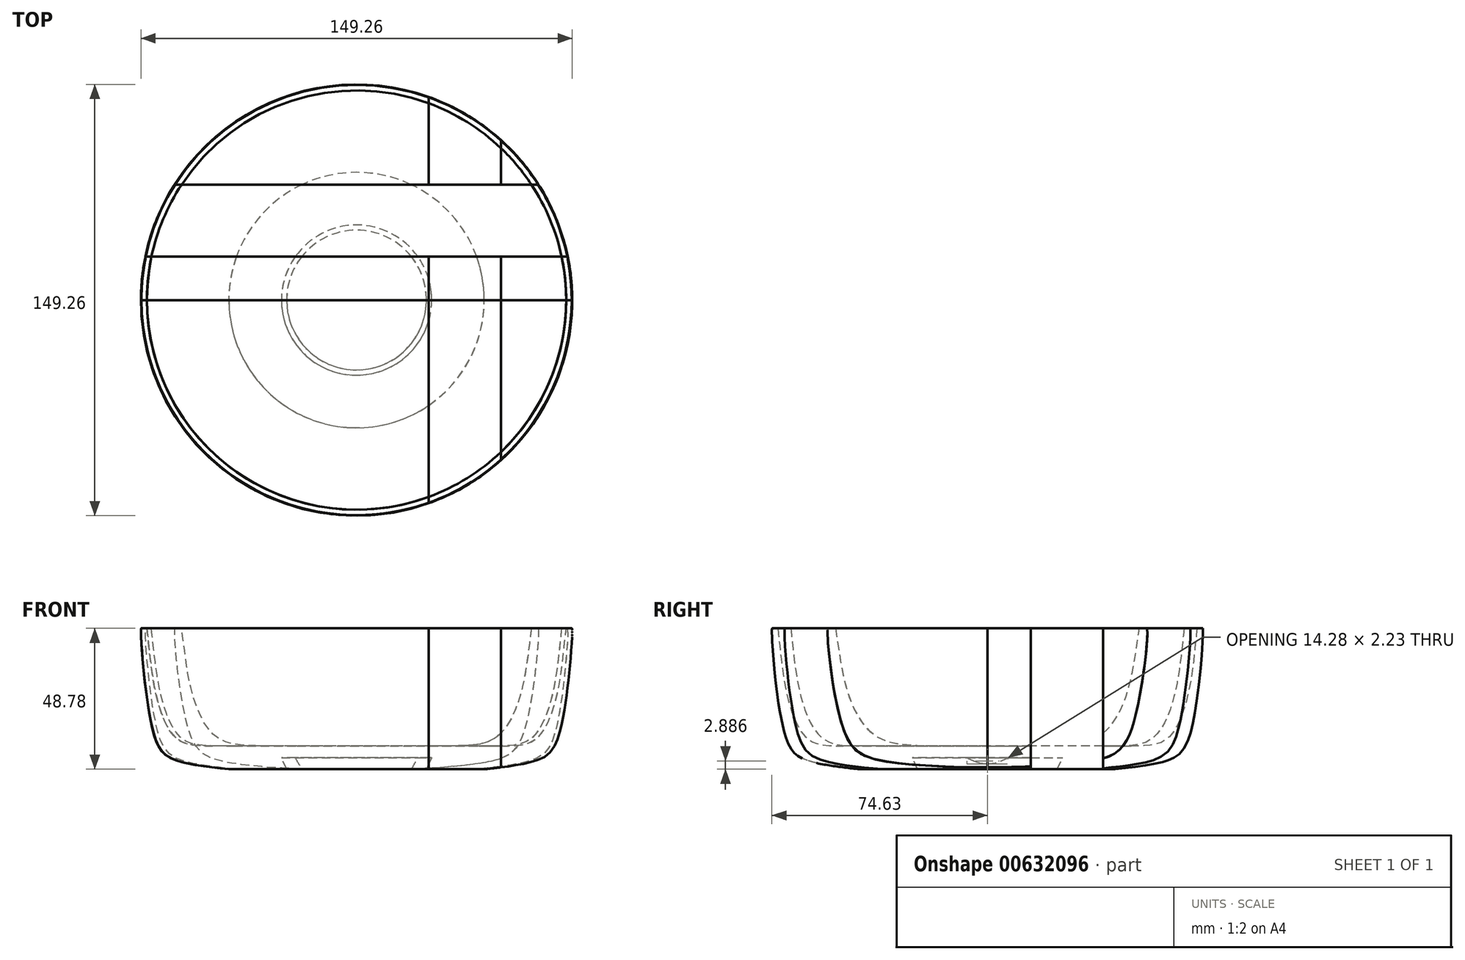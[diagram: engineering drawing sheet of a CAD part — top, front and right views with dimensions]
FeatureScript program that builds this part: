
annotation { "Feature Type Name" : "Feature", "Feature Type Description" : "" }
export const myFeature = defineFeature(function(context is Context, id is Id, definition is map)
    precondition{}
    {
        {
            var Q0;
            Q0=qCreatedBy(makeId("Top.planeOp"),FACE);
            var sketch = newSketch(context, id + "F0", { "sketchPlane" : qUnion([Q0])});
            skLineSegment(sketch, "E0.bottom", {"start": v(0, 0) * mm, "end": v(100, 0) * mm});
            skLineSegment(sketch, "E0.top", {"start": v(0, 25) * mm, "end": v(100, 25) * mm});
            skLineSegment(sketch, "E0.left", {"start": v(0, 0) * mm, "end": v(0, 25) * mm});
            skLineSegment(sketch, "E1.bottom", {"start": v(100, 25) * mm, "end": v(125, 25) * mm});
            skLineSegment(sketch, "E1.top", {"start": v(100, 0) * mm, "end": v(125, 0) * mm});
            skLineSegment(sketch, "E2.bottom", {"start": v(125, 25) * mm, "end": v(160, 25) * mm});
            skLineSegment(sketch, "E2.top", {"start": v(125, 0) * mm, "end": v(160, 0) * mm});
            skLineSegment(sketch, "E2.right", {"start": v(160, 25) * mm, "end": v(160, 0) * mm});
            skLineSegment(sketch, "E3.top", {"start": v(0, 60) * mm, "end": v(100, 60) * mm});
            skLineSegment(sketch, "E3.left", {"start": v(0, 25) * mm, "end": v(0, 60) * mm});
            skLineSegment(sketch, "E3.right", {"start": v(100, 25) * mm, "end": v(100, 60) * mm});
            skLineSegment(sketch, "E4.bottom", {"start": v(100, 60) * mm, "end": v(125, 60) * mm});
            skLineSegment(sketch, "E4.left", {"start": v(100, 60) * mm, "end": v(100, 25) * mm});
            skLineSegment(sketch, "E4.right", {"start": v(125, 60) * mm, "end": v(125, 25) * mm});
            skLineSegment(sketch, "E5.bottom", {"start": v(125, 60) * mm, "end": v(160, 60) * mm});
            skLineSegment(sketch, "E5.right", {"start": v(160, 60) * mm, "end": v(160, 25) * mm});
            skLineSegment(sketch, "E6.top", {"start": v(0, -90) * mm, "end": v(100, -90) * mm});
            skLineSegment(sketch, "E6.left", {"start": v(0, 0) * mm, "end": v(0, -90) * mm});
            skLineSegment(sketch, "E6.right", {"start": v(100, 0) * mm, "end": v(100, -90) * mm});
            skLineSegment(sketch, "E7.top", {"start": v(100, -90) * mm, "end": v(125, -90) * mm});
            skLineSegment(sketch, "E7.right", {"start": v(125, 0) * mm, "end": v(125, -90) * mm});
            skLineSegment(sketch, "E8.top", {"start": v(125, -90) * mm, "end": v(160, -90) * mm});
            skLineSegment(sketch, "E8.right", {"start": v(160, 0) * mm, "end": v(160, -90) * mm});
            skLineSegment(sketch, "E9", {"start": v(0, -15) * mm, "end": v(160, -15) * mm});
            skSolve(sketch);
        }
        {
            var Q0;
            Q0=makeQuery(id+"F0.imprint","IMPRINT",FACE,{"disambiguationData":[TD([[makeQuery(id+"F0.imprint","IMPRINT",EDGE,{"derivedFrom":sQuery(id+"F0.wireOp",EDGE,"E0.top")}),1.0]])]});
            extrude(context, id + "F1", {"entities" : qUnion([Q0]), "depth" : 50 * mm, "offsetDistance" : 25 * mm});
        }
        {
            var Q0;
            Q0=makeQuery(id+"F0.imprint","IMPRINT",FACE,{"disambiguationData":[TD([[makeQuery(id+"F0.imprint","IMPRINT",EDGE,{"derivedFrom":sQuery(id+"F0.wireOp",EDGE,"E4.bottom")}),-1.0]])]});
            extrude(context, id + "F2", {"entities" : qUnion([Q0]), "depth" : 50 * mm, "offsetDistance" : 25 * mm});
        }
        {
            var Q0;
            Q0=makeQuery(id+"F0.imprint","IMPRINT",FACE,{"disambiguationData":[TD([[makeQuery(id+"F0.imprint","IMPRINT",EDGE,{"derivedFrom":sQuery(id+"F0.wireOp",EDGE,"E5.bottom")}),-1.0]])]});
            extrude(context, id + "F3", {"entities" : qUnion([Q0]), "depth" : 50 * mm, "offsetDistance" : 25 * mm});
        }
        {
            var Q0;
            Q0=makeQuery(id+"F0.imprint","IMPRINT",FACE,{"disambiguationData":[TD([[makeQuery(id+"F0.imprint","IMPRINT",EDGE,{"derivedFrom":sQuery(id+"F0.wireOp",EDGE,"E0.left")}),-1.0]])]});
            extrude(context, id + "F4", {"entities" : qUnion([Q0]), "depth" : 50 * mm, "offsetDistance" : 25 * mm});
        }
        {
            var Q0;
            Q0=makeQuery(id+"F0.imprint","IMPRINT",FACE,{"disambiguationData":[TD([[makeQuery(id+"F0.imprint","IMPRINT",EDGE,{"derivedFrom":sQuery(id+"F0.wireOp",EDGE,"E1.left")}),1.0]])]});
            var Q1;
            {var subQ0=sQuery(id+"F0.wireOp",EDGE,"E0.bottom");Q1=makeQuery(id+"F0.imprint","IMPRINT",FACE,{"disambiguationData":[TD([[makeQuery(id+"F0.imprint","IMPRINT",EDGE,{"derivedFrom":subQ0}),-1.0]])]});}
            var Q2;
            {var subQ0=sQuery(id+"F0.wireOp",EDGE,"E2.top");Q2=makeQuery(id+"F0.imprint","IMPRINT",FACE,{"disambiguationData":[TD([[makeQuery(id+"F0.imprint","IMPRINT",EDGE,{"derivedFrom":subQ0}),-1.0]])]});}
            var Q3;
            {var subQ0=sQuery(id+"F0.wireOp",EDGE,"E6.top");Q3=makeQuery(id+"F0.imprint","IMPRINT",FACE,{"disambiguationData":[TD([[makeQuery(id+"F0.imprint","IMPRINT",EDGE,{"derivedFrom":subQ0}),1.0]])]});}
            var Q4;
            {var subQ0=sQuery(id+"F0.wireOp",EDGE,"E8.top");Q4=makeQuery(id+"F0.imprint","IMPRINT",FACE,{"disambiguationData":[TD([[makeQuery(id+"F0.imprint","IMPRINT",EDGE,{"derivedFrom":subQ0}),1.0]])]});}
            extrude(context, id + "F5", {"entities" : qUnion([Q0, Q1, Q2, Q3, Q4]), "depth" : 50 * mm, "offsetDistance" : 25 * mm});
        }
        {
            var Q0;
            {var subQ0=sQuery(id+"F0.wireOp",EDGE,"E1.top");Q0=makeQuery(id+"F0.imprint","IMPRINT",FACE,{"disambiguationData":[TD([[makeQuery(id+"F0.imprint","IMPRINT",EDGE,{"derivedFrom":subQ0}),-1.0]])]});}
            var Q1;
            {var subQ0=sQuery(id+"F0.wireOp",EDGE,"E7.top");Q1=makeQuery(id+"F0.imprint","IMPRINT",FACE,{"disambiguationData":[TD([[makeQuery(id+"F0.imprint","IMPRINT",EDGE,{"derivedFrom":subQ0}),1.0]])]});}
            extrude(context, id + "F6", {"entities" : qUnion([Q0, Q1]), "depth" : 50 * mm, "offsetDistance" : 25 * mm});
        }
        {
            var Q0;
            {var subQ0=sQuery(id+"F0.wireOp",EDGE,"E0.bottom");Q0=makeQuery(id+"F0.imprint","IMPRINT",FACE,{"disambiguationData":[TD([[makeQuery(id+"F0.imprint","IMPRINT",EDGE,{"derivedFrom":subQ0}),-1.0]])]});}
            extrude(context, id + "F7", {"entities" : qUnion([Q0]), "depth" : 50 * mm, "offsetDistance" : 25 * mm});
        }
        {
            var Q0;
            {var subQ0=sQuery(id+"F0.wireOp",EDGE,"E1.top");Q0=makeQuery(id+"F0.imprint","IMPRINT",FACE,{"disambiguationData":[TD([[makeQuery(id+"F0.imprint","IMPRINT",EDGE,{"derivedFrom":subQ0}),-1.0]])]});}
            extrude(context, id + "F8", {"entities" : qUnion([Q0]), "depth" : 50 * mm, "offsetDistance" : 25 * mm});
        }
        {
            var Q0;
            {var subQ0=sQuery(id+"F0.wireOp",EDGE,"E2.top");Q0=makeQuery(id+"F0.imprint","IMPRINT",FACE,{"disambiguationData":[TD([[makeQuery(id+"F0.imprint","IMPRINT",EDGE,{"derivedFrom":subQ0}),-1.0]])]});}
            extrude(context, id + "F9", {"entities" : qUnion([Q0]), "depth" : 50 * mm, "offsetDistance" : 25 * mm});
        }
        {
            var Q0;
            {var subQ0=sQuery(id+"F0.wireOp",EDGE,"E6.top");Q0=makeQuery(id+"F0.imprint","IMPRINT",FACE,{"disambiguationData":[TD([[makeQuery(id+"F0.imprint","IMPRINT",EDGE,{"derivedFrom":subQ0}),1.0]])]});}
            extrude(context, id + "F10", {"entities" : qUnion([Q0]), "depth" : 50 * mm, "offsetDistance" : 25 * mm});
        }
        {
            var Q0;
            {var subQ0=sQuery(id+"F0.wireOp",EDGE,"E7.top");Q0=makeQuery(id+"F0.imprint","IMPRINT",FACE,{"disambiguationData":[TD([[makeQuery(id+"F0.imprint","IMPRINT",EDGE,{"derivedFrom":subQ0}),1.0]])]});}
            extrude(context, id + "F11", {"entities" : qUnion([Q0]), "depth" : 50 * mm, "offsetDistance" : 25 * mm});
        }
        {
            var Q0;
            {var subQ0=sQuery(id+"F0.wireOp",EDGE,"E8.top");Q0=makeQuery(id+"F0.imprint","IMPRINT",FACE,{"disambiguationData":[TD([[makeQuery(id+"F0.imprint","IMPRINT",EDGE,{"derivedFrom":subQ0}),1.0]])]});}
            extrude(context, id + "F12", {"entities" : qUnion([Q0]), "depth" : 50 * mm, "offsetDistance" : 25 * mm});
        }
        {
            var Q0;
            Q0=makeQuery(id+"F7.opExtrude","SWEPT_FACE",FACE,{"disambiguationData":[OSD([sQuery(id+"F0.wireOp",EDGE,"E9")])]});
            var sketch = newSketch(context, id + "F13", { "sketchPlane" : qUnion([Q0])});
            skLineSegment(sketch, "E10", {"start": v(75, 72.12) * mm, "end": v(75, -27.18) * mm, "construction": true});
            skLineSegment(sketch, "E11", {"start": v(75, 4) * mm, "end": v(101, 4) * mm});
            skLineSegment(sketch, "E12", {"start": v(101, 4) * mm, "end": v(99.2, 0) * mm});
            skLineSegment(sketch, "E13", {"start": v(99.2, 0) * mm, "end": v(119.2, 0) * mm});
            skLineSegment(sketch, "E14", {"start": v(75, 8.1) * mm, "end": v(120, 8.1) * mm});
            skFitSpline(sketch, "E15", {"points": [v(119.2, 0) * mm, v(137.89, 3.26) * mm, v(145.42, 13.09) * mm, v(149.54, 48.76) * mm, v(149.46, 48.76) * mm], "startDerivative": vector(68.66, 7.54) * mm, "endDerivative": vector(-4.23, -2.58) * mm});
            skFitSpline(sketch, "E16", {"points": [v(120, 8.1) * mm, v(137.42, 10.74) * mm, v(144.55, 26.48) * mm, v(147.56, 48.76) * mm], "startDerivative": vector(87.08, 0) * mm, "endDerivative": vector(7.06, 60.03) * mm});
            skLineSegment(sketch, "E17", {"start": v(147.56, 48.76) * mm, "end": v(149.46, 48.76) * mm});
            skLineSegment(sketch, "E18", {"start": v(75, 8.1) * mm, "end": v(75, 4) * mm});
            skSolve(sketch);
        }
        {
            var Q0;
            {var subQ0=sQuery(id+"F13.wireOp",EDGE,"E18");Q0=makeQuery(id+"F13.imprint","IMPRINT",FACE,{"disambiguationData":[TD([[makeQuery(id+"F13.imprint","IMPRINT",EDGE,{"derivedFrom":subQ0}),1.0]])]});}
            var Q1;
            {var subQ3=sQuery(id+"F13.wireOp",EDGE,"E15");Q1=makeQuery(id+"F13.imprint","IMPRINT",FACE,{"disambiguationData":[TD([[makeQuery(id+"F13.imprint","IMPRINT",EDGE,{"derivedFrom":subQ3}),1.0]])]});}
            var Q2;
            {var subQ0=sQuery(id+"F13.wireOp",EDGE,"E13");var subQ1=sQuery(id+"F13.wireOp",EDGE,"E12");var subQ2=sQuery(id+"F0.wireOp",EDGE,"E9");var subQ3=makeQuery(id+"F13.imprint","INTERSECT",VERTEX,{"derivedFrom":[makeQuery(id+"F7.opExtrude","CAP_EDGE",EDGE,{"disambiguationData":[OSD([subQ2])],"isStart":true}),subQ1,subQ0]});Q2=makeQuery(id+"F13.imprint","IMPRINT",FACE,{"disambiguationData":[TD([[makeQuery(id+"F13.imprint","IMPRINT",EDGE,{"disambiguationData":[TD([[subQ3,1.0]])],"derivedFrom":subQ1}),1.0]])]});}
            var Q3;
            Q3=sQuery(id+"F13.wireOp",EDGE,"E10");
            revolve(context, id + "F14", {"operationType" : NewBodyOperationType.INTERSECT, "entities" : qUnion([Q0, Q1, Q2]), "axis" : qUnion([Q3]), "revolveType" : RevolveType.FULL, "oppositeDirection" : true});
        }
    });
